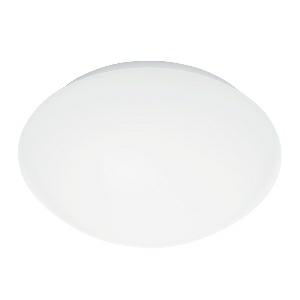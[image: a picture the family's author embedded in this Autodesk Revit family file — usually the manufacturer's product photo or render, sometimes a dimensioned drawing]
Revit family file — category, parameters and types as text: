
# Revit family: rs_pro_led_p2_058586
name_source: partatom
category: Leuchten
revit_build: Autodesk Revit 2016 (Build: 20190508_0715(x64)
units: mm (PartAtom-declared; Revit-internal decimal feet)

## family parameters
Basisbauteil = Fläche
Beim Laden mit Abzugskörper schneiden = Nein
Bemaßung runder Anschluss = Durchmesser verwenden
Gemeinsam genutzt = Nein
Lichtquelle = Nein
Raumberechnungspunkt = Nein
Teiletyp = Normal

## types (1)
- RS PRO LED P2 (1 x , 1730 lm, 3000 K)
    Beschreibung = Dimensions (Ø x H): 320 x 110 mm; Mains power supply: 220 – 240 V / 50 – 60 Hz; Sensor Technology: High frequency; Transmitter power: < 1 mW; HF-system: 5,8 GHz; Output: 16 W; Interconnection: Yes; Type of interconnection: Master/master; Luminous flux: 1730 lm; Luminous flux, emergency light: 38 lm; Colour temperature: 3000 K; Colour variation LED: SDCM3; Colour Rendering Index CRI: 80-89; With lamp: Yes, STEINEL LED system; Lamp: LED cannot be replaced; LED life expectancy (max. °C): 50000 h; Drop in luminous flux in accordance with LM80: L80B10; Base: without; LED cooling system: Passive Thermo Control; With motion detector: Yes; Detection: also through glass, wood and stud walls; Detection angle: 360 °; Angle of aperture: 160 °; Capability of masking out individual segments: Yes; Electronic scalability: Yes; Mechanical scalability: No; Reach, radial: Ø 8 m (50 m²); Reach, tangential: Ø 8 m (50 m²); Continuous light: selectable, 4h; Photo-cell controller: Yes; Twilight setting: 2 – 2000 lx; Time setting: 5 sec – 15 min; Basic light level function: Yes; Basic light level function time: 10/30 min, all night; Soft light start: Yes; Impact resistance: IK03; IP-rating: IP54; Protection class: II; Ambient temperature: 10 – 40 °C; Housing material: Plastic; Cover material: Plastic, opal; Manufacturer's Warranty: 5 years; Settings via: Potentiometers; With remote control: No; Version: Emergency light - warm white; PU1, EAN: 4007841058586
    Color Rendering = 80-89
    Color Temperature = 3000 K
    Frequency = 60 Hz, 50 Hz
    Height = 0 mm  [stored 0 ft]
    Hersteller = Steinel
    Lamp Light Flux = 1730 lm
    Lamp count = 1
    Lampe = 1 x
    Length = 320 mm
    Luminous efficacy = 0 lm/W
    ModVariant = Nein
    Modell = 058586
    Mounting Type = Surface mounted
    Number of Poles = 1
    OnlyDefault = Ja
    Power Factor = 1
    Product Name = RS PRO LED P2
    Product group = Sensor-switched indoor light
    ProductGroupID = 30
    Protection Class = Protection class II
    Protection Degree = IP 54
    RlxData = <blob elided: 32925 chars, md5=7e8008dd>
    Scheinlast = 16 VA
    Socket = socket
    Standby Power = 0 W
    System Light Flux = 0 lm
    System Power = 16 W
    Typenbild = produkt1_058586.jpg
    Typenkommentare = Product without accessories
    URL = http://relux.com
    VarID = ---
    Voltage = 0 V
    Vorgabe-Ansicht = 1800 mm
    Weight = 0.00 kg
    Width = 0 mm  [stored 0 ft]

note: [stored X ft] marks values corroborated as IEEE doubles in the binary element streams (Revit-internal decimal feet)

## geometry (parser evidence)
native form markers: Blend x4, Sweep x11
no freeform markers — native parametric forms only
